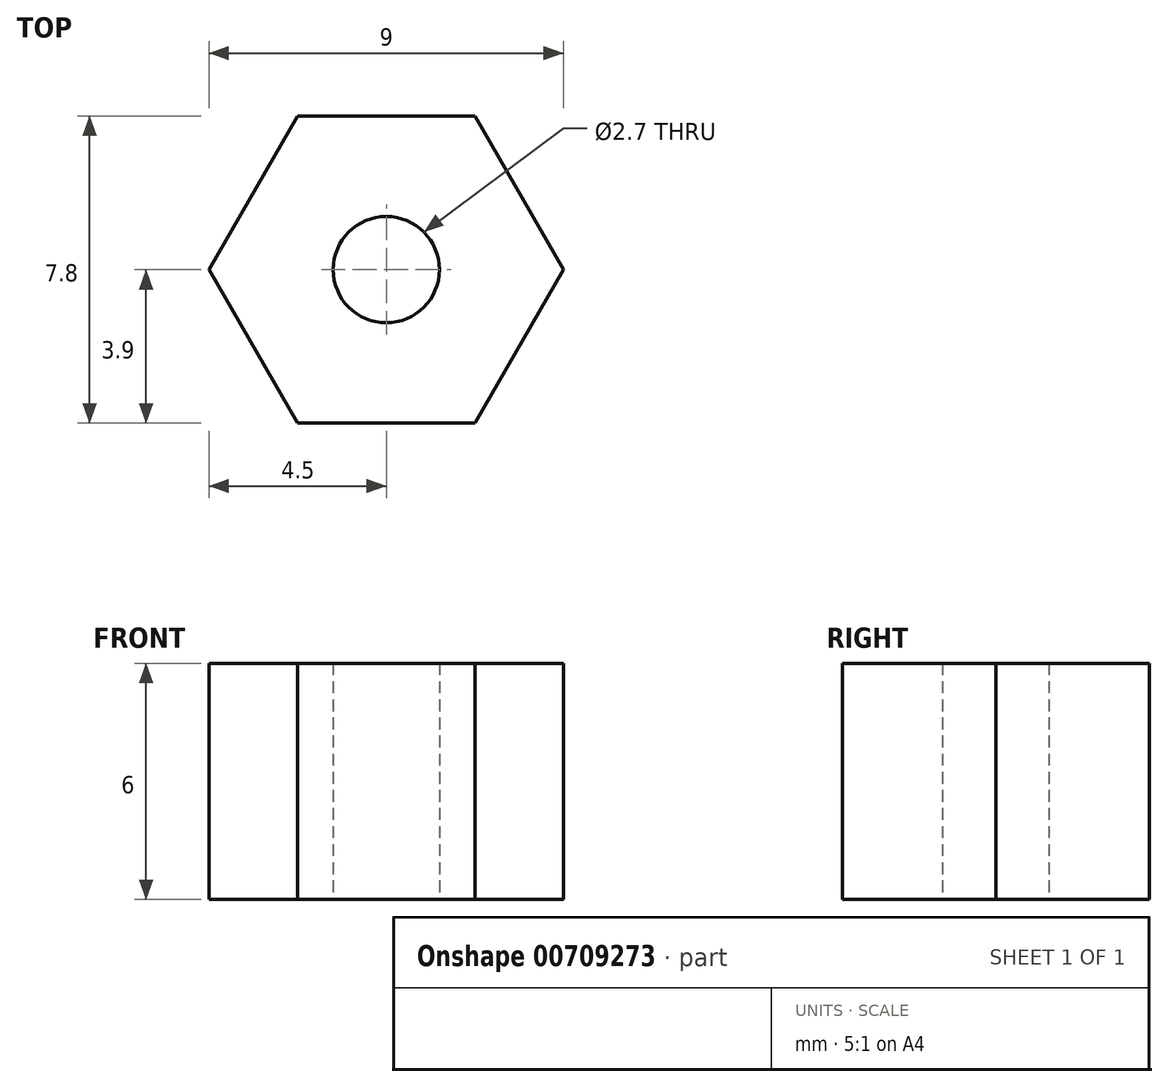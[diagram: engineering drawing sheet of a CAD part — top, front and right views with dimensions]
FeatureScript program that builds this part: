
annotation { "Feature Type Name" : "Feature", "Feature Type Description" : "" }
export const myFeature = defineFeature(function(context is Context, id is Id, definition is map)
    precondition{}
    {
        {
            var Q0;
            Q0=qCreatedBy(makeId("Top.planeOp"),FACE);
            var sketch = newSketch(context, id + "F0", { "sketchPlane" : qUnion([Q0])});
            skCircle(sketch, "E0.cCircle", {"center": v(0, 0) * mm, "radius": 4.5 * mm, "construction": true});
            skLineSegment(sketch, "E0.0", {"start": v(4.5, 0) * mm, "end": v(2.25, -3.9) * mm});
            skLineSegment(sketch, "E0.1", {"start": v(2.25, -3.9) * mm, "end": v(-2.25, -3.9) * mm});
            skLineSegment(sketch, "E0.2", {"start": v(-2.25, -3.9) * mm, "end": v(-4.5, 0) * mm});
            skLineSegment(sketch, "E0.3", {"start": v(-4.5, 0) * mm, "end": v(-2.25, 3.9) * mm});
            skLineSegment(sketch, "E0.4", {"start": v(-2.25, 3.9) * mm, "end": v(2.25, 3.9) * mm});
            skLineSegment(sketch, "E0.5", {"start": v(2.25, 3.9) * mm, "end": v(4.5, 0) * mm});
            skCircle(sketch, "E1", {"center": v(0, 0) * mm, "radius": 1.5 * mm});
            skSolve(sketch);
        }
        {
            var Q0;
            Q0=makeQuery(id+"F0.imprint","IMPRINT",FACE,{"disambiguationData":[TD([[makeQuery(id+"F0.imprint","IMPRINT",EDGE,{"derivedFrom":sQuery(id+"F0.wireOp",EDGE,"E0.0")}),-1.0]])]});
            var Q1;
            Q1=makeQuery(id+"F0.imprint","IMPRINT",FACE,{"disambiguationData":[TD([[makeQuery(id+"F0.imprint","IMPRINT",EDGE,{"derivedFrom":sQuery(id+"F0.wireOp",EDGE,"E1")}),1.0]])]});
            extrude(context, id + "F1", {"entities" : qUnion([Q0, Q1]), "depth" : 6 * mm, "offsetDistance" : 25 * mm});
        }
        {
            var Q0;
            Q0=sQuery(id+"F0.wireOp",VERTEX,"E1.center");
            var Q1;
            Q1=makeQuery(id+"F1.opExtrude","SWEPT_BODY",BODY,{"disambiguationData":[OSD([sQuery(id+"F0.wireOp",EDGE,"E0.0"),sQuery(id+"F0.wireOp",EDGE,"E0.1"),sQuery(id+"F0.wireOp",EDGE,"E0.2"),sQuery(id+"F0.wireOp",EDGE,"E0.3"),sQuery(id+"F0.wireOp",EDGE,"E0.4"),sQuery(id+"F0.wireOp",EDGE,"E0.5")])]});
            hole(context, id + "F2", {"style" : HoleStyle.SIMPLE, "endStyle" : HoleEndStyle.THROUGH, "oppositeDirection" : true, "standardTappedOrClearance" : lookupTablePath({ "standard" : "ISO", "engagement" : "50%", "pitch" : "0.5 mm", "size" : "M3", "type" : "Tapped" }), "standardBlindInLast" : lookupTablePath({ "standard" : "ISO", "engagement" : "50%", "pitch" : "0.5 mm", "size" : "M3", "type" : "Tapped" }), "holeDiameter" : 2.7 * mm, "majorDiameter" : 3 * mm, "showTappedDepth" : true, "isTappedThrough" : true, "tappedDepth" : 5 * mm, "tapClearance" : 0, "locations" : qUnion([Q0]), "scope" : qUnion([Q1])});
        }
    });
